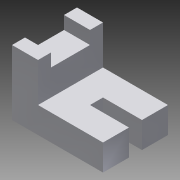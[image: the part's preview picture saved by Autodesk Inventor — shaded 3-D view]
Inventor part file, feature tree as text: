
AUTODESK INVENTOR PART (.ipt)
format: ipt  version: 2015 (Build 190159000, 159)  size: 100,352 bytes
history: native  units: in
note: dims shown in document units (in); Inventor stores cm internally (conversion verified against a paired STEP export)
features: extrude x3, sketch x3
ambient origin geometry x8: Origin, YZ Plane, XZ Plane, XY Plane, X Axis, Y Axis, Z Axis, Center Point
bodies: Solid1 (feature_tree)
feature tree (6):
  extrude  "Extrusion1"  Depth=1.75in
  extrude  "Extrusion2"  Depth=0.5in
  extrude  "Extrusion3"  Depth=1.25in TaperAngle=0.0deg
  sketch  "Sketch1"  dims[d0=1.25in d1=1.75in]
  sketch  "Sketch2"  dims[d2=0.75in d3=0.5in]
  sketch  "Sketch3"  dims[d4=0.5in d5=1.25in d6=0.0in d7=0.25in d8=0.75in d9=0.25in d10=1.25in d11=0.0in d12=0.5in d13=0.5in d16=0.25in d17=0.75in d18=0.0in]
